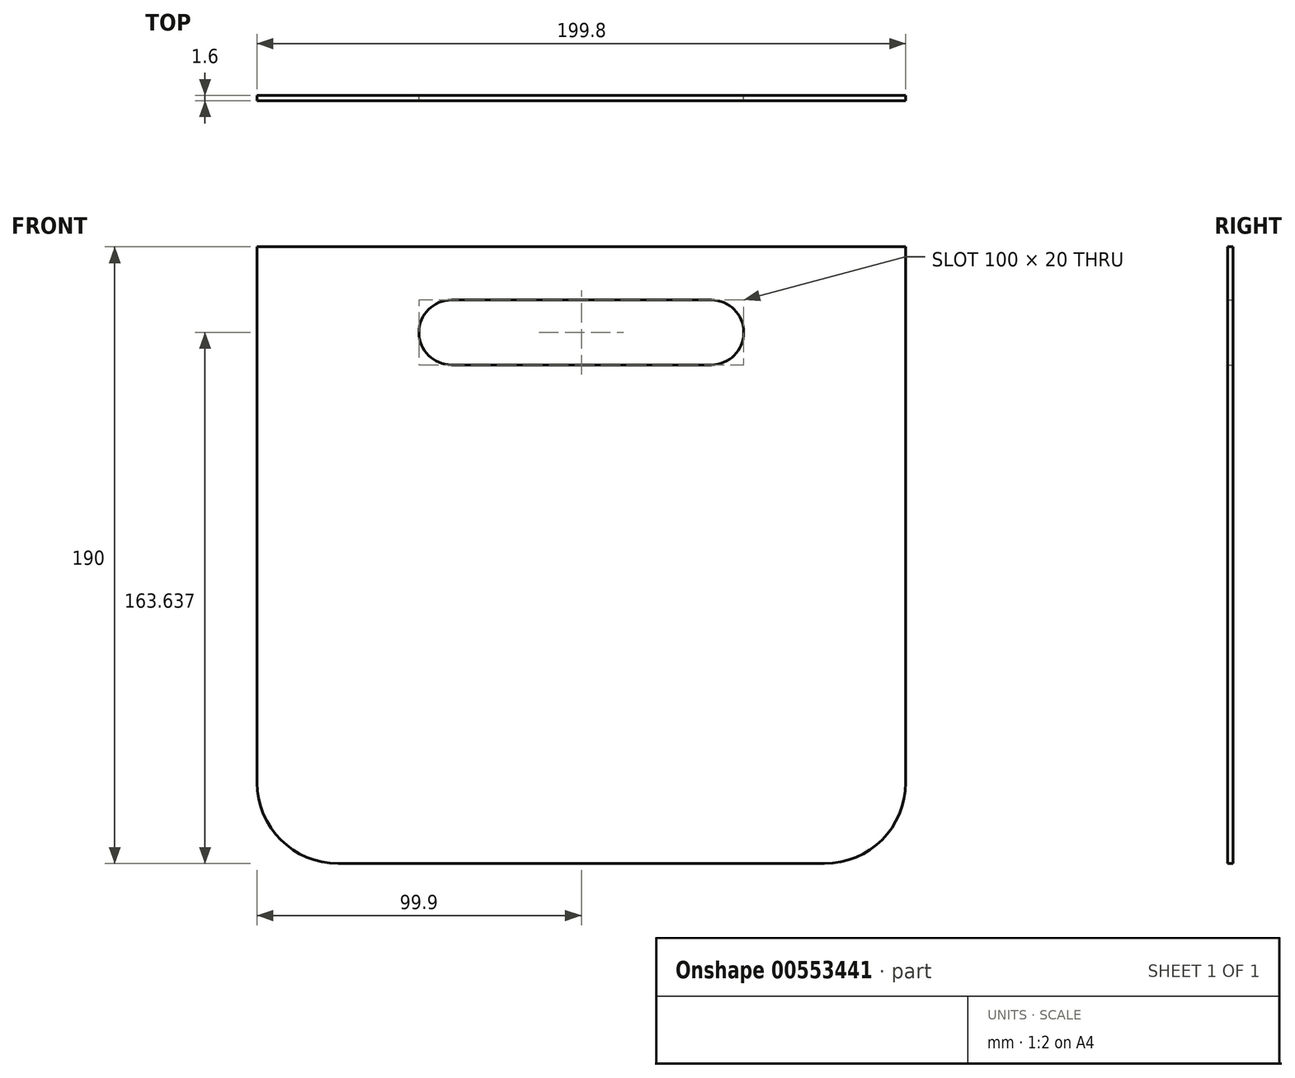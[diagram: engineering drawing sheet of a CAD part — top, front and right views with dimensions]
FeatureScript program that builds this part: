
annotation { "Feature Type Name" : "Feature", "Feature Type Description" : "" }
export const myFeature = defineFeature(function(context is Context, id is Id, definition is map)
    precondition{}
    {
        {
            var Q0;
            Q0=qCreatedBy(makeId("Front.planeOp"),FACE);
            var sketch = newSketch(context, id + "F0", { "sketchPlane" : qUnion([Q0])});
            skLineSegment(sketch, "E0.top", {"start": v(-74.9, -95) * mm, "end": v(74.9, -95) * mm});
            skLineSegment(sketch, "E0.left", {"start": v(-99.9, 95) * mm, "end": v(-99.9, -70) * mm});
            skLineSegment(sketch, "E0.right", {"start": v(99.9, 95) * mm, "end": v(99.9, -70) * mm});
            skPoint(sketch, "E0.middle", {"position": v(0, 0) * mm});
            skPoint(sketch, "E1.visualSharp", {"position": v(-99.9, -95) * mm});
            skArc(sketch, "E1.filletArc", {"start": v(-99.9, -70) * mm, "mid": v(-92.58, -87.68) * mm, "end": v(-74.9, -95) * mm});
            skPoint(sketch, "E2.visualSharp", {"position": v(99.9, -95) * mm});
            skArc(sketch, "E2.filletArc", {"start": v(74.9, -95) * mm, "mid": v(92.58, -87.68) * mm, "end": v(99.9, -70) * mm});
            skLineSegment(sketch, "E3", {"start": v(-99.9, 95) * mm, "end": v(99.9, 95) * mm});
            skLineSegment(sketch, "E4", {"start": v(0, 0) * mm, "end": v(0, 137.27) * mm, "construction": true});
            skLineSegment(sketch, "E5.bottom", {"start": v(40, 58.64) * mm, "end": v(0, 58.64) * mm});
            skLineSegment(sketch, "E5.top", {"start": v(40, 78.64) * mm, "end": v(0, 78.64) * mm});
            skPoint(sketch, "E5.middle", {"position": v(0, 68.64) * mm});
            skPoint(sketch, "E6.orphan", {"position": v(-40, 78.64) * mm});
            skPoint(sketch, "E7.orphan", {"position": v(-40, 58.64) * mm});
            skArc(sketch, "E8", {"start": v(40, 58.64) * mm, "mid": v(50, 68.64) * mm, "end": v(40, 78.64) * mm});
            skLineSegment(sketch, "E9.MirrorCS", {"start": v(-40, 78.64) * mm, "end": v(0, 78.64) * mm});
            skArc(sketch, "E10.MirrorCS", {"start": v(-40, 58.64) * mm, "mid": v(-50, 68.64) * mm, "end": v(-40, 78.64) * mm});
            skLineSegment(sketch, "E11.MirrorCS", {"start": v(-40, 58.64) * mm, "end": v(0, 58.64) * mm});
            skSolve(sketch);
        }
        {
            var Q0;
            Q0=makeQuery(id+"F0.imprint","IMPRINT",FACE,{"disambiguationData":[TD([[makeQuery(id+"F0.imprint","IMPRINT",EDGE,{"derivedFrom":sQuery(id+"F0.wireOp",EDGE,"E0.top")}),1.0]])]});
            extrude(context, id + "F1", {"entities" : qUnion([Q0]), "endBound" : BoundingType.SYMMETRIC, "depth" : 1.6 * mm, "offsetDistance" : 25 * mm});
        }
    });
